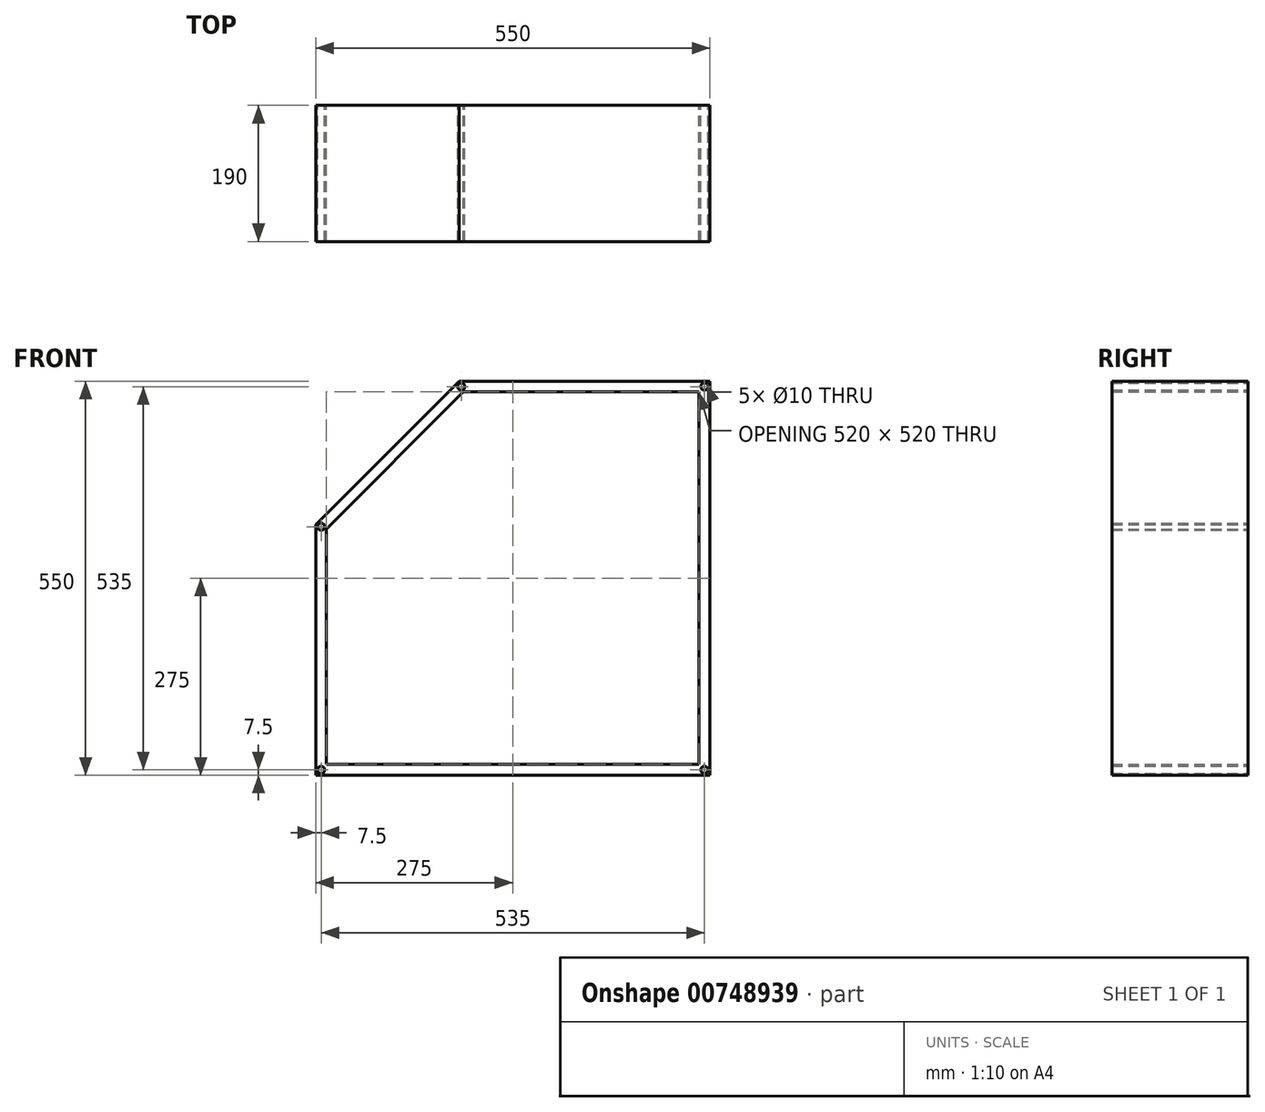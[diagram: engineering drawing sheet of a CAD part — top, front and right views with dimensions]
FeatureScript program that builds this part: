
annotation { "Feature Type Name" : "Feature", "Feature Type Description" : "" }
export const myFeature = defineFeature(function(context is Context, id is Id, definition is map)
    precondition{}
    {
        {
            var Q0;
            Q0=qCreatedBy(makeId("Front.planeOp"),FACE);
            var sketch = newSketch(context, id + "F0", { "sketchPlane" : qUnion([Q0])});
            skLineSegment(sketch, "E0.top", {"start": v(-275, -275) * mm, "end": v(275, -275) * mm});
            skLineSegment(sketch, "E0.right", {"start": v(275, 275) * mm, "end": v(275, -275) * mm});
            skPoint(sketch, "E0.middle", {"position": v(0, 0) * mm});
            skLineSegment(sketch, "E1", {"start": v(-75, 275) * mm, "end": v(275, 275) * mm});
            skLineSegment(sketch, "E2", {"start": v(-275, -275) * mm, "end": v(-275, 75) * mm});
            skLineSegment(sketch, "E3", {"start": v(275, 275) * mm, "end": v(-75, 275) * mm});
            skLineSegment(sketch, "E4", {"start": v(-75, 275) * mm, "end": v(-275, 75) * mm});
            skPoint(sketch, "E5.orphan", {"position": v(-275, 275) * mm});
            skLineSegment(sketch, "E6.0", {"start": v(-260, -260) * mm, "end": v(-260, 68.79) * mm});
            skLineSegment(sketch, "E6.1", {"start": v(-68.79, 260) * mm, "end": v(-260, 68.79) * mm});
            skLineSegment(sketch, "E6.2", {"start": v(-260, -260) * mm, "end": v(260, -260) * mm});
            skLineSegment(sketch, "E6.3", {"start": v(260, 260) * mm, "end": v(260, -260) * mm});
            skLineSegment(sketch, "E6.4", {"start": v(260, 260) * mm, "end": v(-68.79, 260) * mm});
            skLineSegment(sketch, "E7", {"start": v(260, 260) * mm, "end": v(260, -35) * mm});
            skLineSegment(sketch, "E8", {"start": v(-275, 275) * mm, "end": v(-175, 175) * mm, "construction": true});
            skCircle(sketch, "E9", {"center": v(-267.5, 71.9) * mm, "radius": 5 * mm});
            skCircle(sketch, "E10", {"center": v(-267.5, -267.5) * mm, "radius": 5 * mm});
            skCircle(sketch, "E11", {"center": v(267.5, -267.5) * mm, "radius": 5 * mm});
            skCircle(sketch, "E12.MirrorC", {"center": v(-71.9, 267.5) * mm, "radius": 5 * mm});
            skCircle(sketch, "E13.MirrorC", {"center": v(267.5, 267.5) * mm, "radius": 5 * mm});
            skLineSegment(sketch, "E14.trimOffspring", {"start": v(275, -275) * mm, "end": v(391.98, -391.98) * mm, "construction": true});
            skLineSegment(sketch, "E15", {"start": v(47.8, -47.8) * mm, "end": v(-164.4, -260) * mm, "construction": true});
            skLineSegment(sketch, "E16", {"start": v(47.8, -47.8) * mm, "end": v(260, 164.4) * mm, "construction": true});
            skLineSegment(sketch, "E17", {"start": v(260, -260) * mm, "end": v(47.8, -47.8) * mm, "construction": true});
            skLineSegment(sketch, "E18", {"start": v(-164.4, 164.4) * mm, "end": v(47.8, -47.8) * mm, "construction": true});
            skCircle(sketch, "E19", {"center": v(153.9, -153.9) * mm, "radius": 65 * mm, "construction": true});
            skCircle(sketch, "E20", {"center": v(-58.3, 58.3) * mm, "radius": 65 * mm, "construction": true});
            skLineSegment(sketch, "E21", {"start": v(260, 130) * mm, "end": v(-35, 130) * mm});
            skLineSegment(sketch, "E22", {"start": v(-35, 130) * mm, "end": v(-35, 260) * mm});
            skSolve(sketch);
        }
        {
            var Q0;
            Q0 = qSketchRegion(id + "F0", true);
            extrude(context, id + "F1", {"entities" : qUnion([Q0]), "depth" : 190 * mm, "offsetDistance" : 25 * mm, "symmetric" : true});
        }
    });
